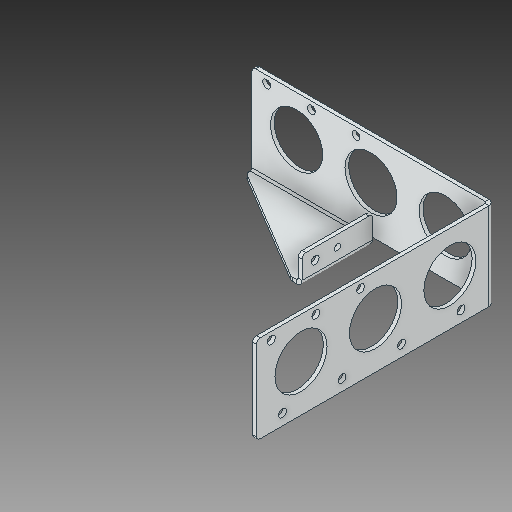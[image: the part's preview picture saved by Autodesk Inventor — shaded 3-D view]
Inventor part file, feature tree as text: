
AUTODESK INVENTOR PART (.ipt)
format: ipt  version: 2019 (Build 230136000, 136)  size: 164,864 bytes
history: native  units: in
note: dims shown in document units (in); Inventor stores cm internally (conversion verified against a paired STEP export)
features: fillet x1
ambient origin geometry x8: Origin, YZ Plane, XZ Plane, XY Plane, X Axis, Y Axis, Z Axis, Center Point
bodies: Solid1 (feature_tree)
feature tree (1):
  fillet  "Fillet1"  [1 undecoded]
note: 1 required parameter value undecoded (feature->parameter linkage not recoverable at this tier; creation-order binding heuristic only, values carry confidence <= 0.55)
